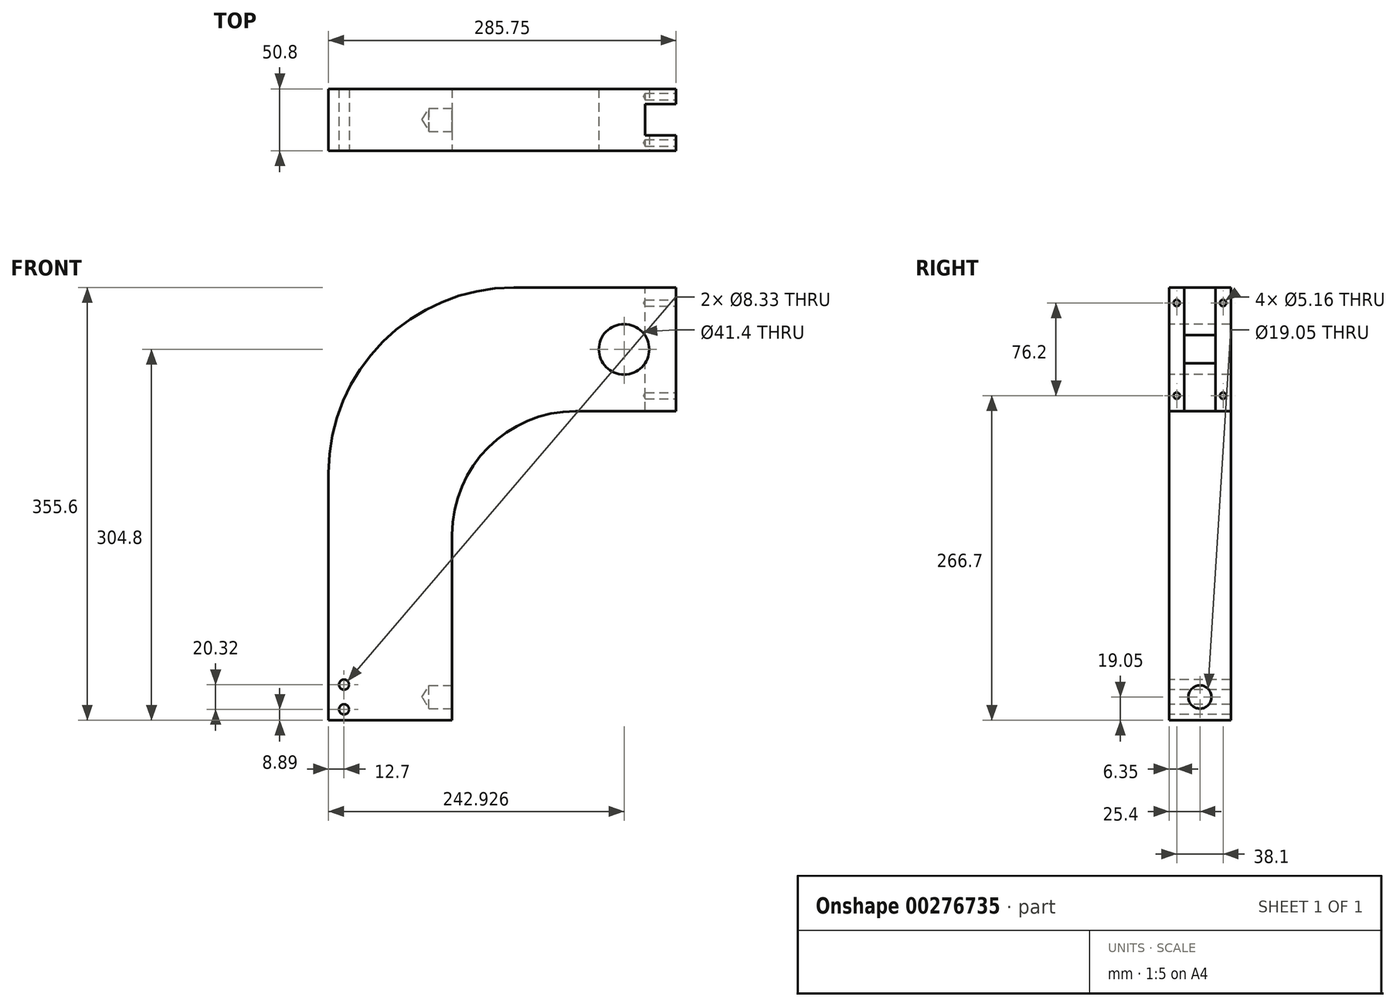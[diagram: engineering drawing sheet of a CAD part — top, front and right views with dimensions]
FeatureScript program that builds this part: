
annotation { "Feature Type Name" : "Feature", "Feature Type Description" : "" }
export const myFeature = defineFeature(function(context is Context, id is Id, definition is map)
    precondition{}
    {
        {
            var Q0;
            Q0=qCreatedBy(makeId("Front.planeOp"),FACE);
            var sketch = newSketch(context, id + "F0", { "sketchPlane" : qUnion([Q0])});
            skLineSegment(sketch, "E0", {"start": v(0, 0) * mm, "end": v(0, 203.2) * mm});
            skLineSegment(sketch, "E1", {"start": v(152.4, 355.6) * mm, "end": v(285.75, 355.6) * mm});
            skLineSegment(sketch, "E2", {"start": v(285.75, 355.6) * mm, "end": v(285.75, 254) * mm});
            skLineSegment(sketch, "E3", {"start": v(101.6, 0) * mm, "end": v(0, 0) * mm});
            skLineSegment(sketch, "E4", {"start": v(285.75, 254) * mm, "end": v(203.2, 254) * mm});
            skLineSegment(sketch, "E5", {"start": v(101.6, 0) * mm, "end": v(101.6, 152.4) * mm});
            skPoint(sketch, "E6.visualSharp", {"position": v(0, 355.6) * mm});
            skArc(sketch, "E6.filletArc", {"start": v(152.4, 355.6) * mm, "mid": v(44.64, 310.96) * mm, "end": v(0, 203.2) * mm});
            skPoint(sketch, "E7.visualSharp", {"position": v(101.6, 254) * mm});
            skArc(sketch, "E7.filletArc", {"start": v(203.2, 254) * mm, "mid": v(131.36, 224.24) * mm, "end": v(101.6, 152.4) * mm});
            skSolve(sketch);
        }
        {
            var Q0;
            Q0 = qSketchRegion(id + "F0", true);
            extrude(context, id + "F1", {"entities" : qUnion([Q0]), "oppositeDirection" : true, "depth" : 50.8 * mm});
        }
        {
            var Q0;
            Q0=makeQuery(id+"F1.opExtrude","CAP_FACE",FACE,{"disambiguationData":[OSD([sQuery(id+"F0.wireOp",EDGE,"E0"),sQuery(id+"F0.wireOp",EDGE,"E1"),sQuery(id+"F0.wireOp",EDGE,"E2"),sQuery(id+"F0.wireOp",EDGE,"E3"),sQuery(id+"F0.wireOp",EDGE,"E4"),sQuery(id+"F0.wireOp",EDGE,"E5"),sQuery(id+"F0.wireOp",EDGE,"E6.filletArc"),sQuery(id+"F0.wireOp",EDGE,"E7.filletArc")])],"isStart":true});
            var sketch = newSketch(context, id + "F2", { "sketchPlane" : qUnion([Q0])});
            skPoint(sketch, "E8", {"position": v(12.7, 29.21) * mm});
            skPoint(sketch, "E9", {"position": v(12.7, 8.9) * mm});
            skSolve(sketch);
        }
        {
            var Q0;
            Q0=sQuery(id+"F2.wireOp",VERTEX,"E8");
            var Q1;
            Q1=sQuery(id+"F2.wireOp",VERTEX,"E9");
            var Q2;
            Q2=makeQuery(id+"F1.opExtrude","SWEPT_BODY",BODY,{"disambiguationData":[OSD([sQuery(id+"F0.wireOp",EDGE,"E0"),sQuery(id+"F0.wireOp",EDGE,"E1"),sQuery(id+"F0.wireOp",EDGE,"E2"),sQuery(id+"F0.wireOp",EDGE,"E3"),sQuery(id+"F0.wireOp",EDGE,"E4"),sQuery(id+"F0.wireOp",EDGE,"E5"),sQuery(id+"F0.wireOp",EDGE,"E6.filletArc"),sQuery(id+"F0.wireOp",EDGE,"E7.filletArc")])]});
            hole(context, id + "F3", {"style" : HoleStyle.SIMPLE, "endStyle" : HoleEndStyle.THROUGH, "holeDiameter" : 8.33 * mm, "tappedDepth" : 12.7 * mm, "tapClearance" : 3, "locations" : qUnion([Q0, Q1]), "scope" : qUnion([Q2])});
        }
        {
            var Q0;
            Q0=makeQuery(id+"F1.opExtrude","SWEPT_FACE",FACE,{"disambiguationData":[OSD([sQuery(id+"F0.wireOp",EDGE,"E5")])]});
            var sketch = newSketch(context, id + "F4", { "sketchPlane" : qUnion([Q0])});
            skPoint(sketch, "E10", {"position": v(25.4, 19.05) * mm});
            skSolve(sketch);
        }
        {
            var Q0;
            Q0=sQuery(id+"F4.wireOp",VERTEX,"E10");
            var Q1;
            Q1=makeQuery(id+"F1.opExtrude","SWEPT_BODY",BODY,{"disambiguationData":[OSD([sQuery(id+"F0.wireOp",EDGE,"E0"),sQuery(id+"F0.wireOp",EDGE,"E1"),sQuery(id+"F0.wireOp",EDGE,"E2"),sQuery(id+"F0.wireOp",EDGE,"E3"),sQuery(id+"F0.wireOp",EDGE,"E4"),sQuery(id+"F0.wireOp",EDGE,"E5"),sQuery(id+"F0.wireOp",EDGE,"E6.filletArc"),sQuery(id+"F0.wireOp",EDGE,"E7.filletArc")])]});
            hole(context, id + "F5", {"style" : HoleStyle.SIMPLE, "endStyle" : HoleEndStyle.BLIND, "holeDiameter" : 19.05 * mm, "holeDepth" : 19.05 * mm, "tappedDepth" : 12.7 * mm, "tapClearance" : 3, "locations" : qUnion([Q0]), "scope" : qUnion([Q1])});
        }
        {
            var Q0;
            Q0=makeQuery(id+"F1.opExtrude","SWEPT_FACE",FACE,{"disambiguationData":[OSD([sQuery(id+"F0.wireOp",EDGE,"E1")])]});
            var sketch = newSketch(context, id + "F6", { "sketchPlane" : qUnion([Q0])});
            skLineSegment(sketch, "E11", {"start": v(285.75, 25.4) * mm, "end": v(0, 25.4) * mm, "construction": true});
            skLineSegment(sketch, "E12.bottom", {"start": v(285.75, 38.23) * mm, "end": v(260.1, 38.23) * mm});
            skLineSegment(sketch, "E12.top", {"start": v(285.75, 12.57) * mm, "end": v(260.1, 12.57) * mm});
            skLineSegment(sketch, "E12.left", {"start": v(285.75, 38.23) * mm, "end": v(285.75, 12.57) * mm});
            skLineSegment(sketch, "E12.right", {"start": v(260.1, 38.23) * mm, "end": v(260.1, 12.57) * mm});
            skSolve(sketch);
        }
        {
            var Q0;
            Q0 = qSketchRegion(id + "F6", true);
            extrude(context, id + "F7", {"entities" : qUnion([Q0]), "operationType" : NewBodyOperationType.REMOVE, "endBound" : BoundingType.THROUGH_ALL, "oppositeDirection" : true, "depth" : 25.4 * mm});
        }
        {
            var Q0;
            Q0=makeQuery(id+"F1.opExtrude","CAP_FACE",FACE,{"disambiguationData":[OSD([sQuery(id+"F0.wireOp",EDGE,"E0"),sQuery(id+"F0.wireOp",EDGE,"E1"),sQuery(id+"F0.wireOp",EDGE,"E2"),sQuery(id+"F0.wireOp",EDGE,"E3"),sQuery(id+"F0.wireOp",EDGE,"E4"),sQuery(id+"F0.wireOp",EDGE,"E5"),sQuery(id+"F0.wireOp",EDGE,"E6.filletArc"),sQuery(id+"F0.wireOp",EDGE,"E7.filletArc")])],"isStart":true});
            var sketch = newSketch(context, id + "F8", { "sketchPlane" : qUnion([Q0])});
            skCircle(sketch, "E13", {"center": v(242.93, 304.8) * mm, "radius": 20.7 * mm});
            skSolve(sketch);
        }
        {
            var Q0;
            Q0 = qSketchRegion(id + "F8", true);
            extrude(context, id + "F9", {"entities" : qUnion([Q0]), "operationType" : NewBodyOperationType.REMOVE, "endBound" : BoundingType.THROUGH_ALL, "oppositeDirection" : true, "depth" : 25.4 * mm});
        }
        {
            var Q0;
            {var subQ1=sQuery(id+"F0.wireOp",EDGE,"E2");Q0=makeQuery(id+"F7.boolean.opBoolean","SPLIT",FACE,{"disambiguationData":[TD([makeQuery(id+"F7.opExtrude","SWEPT_FACE",FACE,{"disambiguationData":[OSD([sQuery(id+"F6.wireOp",EDGE,"E12.top")])]})])],"derivedFrom":makeQuery(id+"F1.opExtrude","SWEPT_FACE",FACE,{"disambiguationData":[OSD([subQ1])]})});}
            var sketch = newSketch(context, id + "F10", { "sketchPlane" : qUnion([Q0])});
            skPoint(sketch, "E14", {"position": v(6.35, 342.9) * mm});
            skPoint(sketch, "E15", {"position": v(44.45, 342.9) * mm});
            skPoint(sketch, "E16", {"position": v(6.35, 266.7) * mm});
            skPoint(sketch, "E17", {"position": v(44.45, 266.7) * mm});
            skLineSegment(sketch, "E18.0", {"start": v(50.8, 0) * mm, "end": v(0, 0) * mm, "construction": true});
            skLineSegment(sketch, "E19.0", {"start": v(0, 355.6) * mm, "end": v(0, 254) * mm, "construction": true});
            skLineSegment(sketch, "E20", {"start": v(25.4, 0) * mm, "end": v(25.4, 364.03) * mm, "construction": true});
            skLineSegment(sketch, "E21", {"start": v(0, 304.8) * mm, "end": v(96.81, 304.8) * mm, "construction": true});
            skSolve(sketch);
        }
        {
            var Q0;
            Q0=sQuery(id+"F10.wireOp",VERTEX,"E14");
            var Q1;
            Q1=sQuery(id+"F10.wireOp",VERTEX,"E15");
            var Q2;
            Q2=sQuery(id+"F10.wireOp",VERTEX,"E16");
            var Q3;
            Q3=sQuery(id+"F10.wireOp",VERTEX,"E17");
            var Q4;
            Q4=makeQuery(id+"F1.opExtrude","SWEPT_BODY",BODY,{"disambiguationData":[OSD([sQuery(id+"F0.wireOp",EDGE,"E0"),sQuery(id+"F0.wireOp",EDGE,"E1"),sQuery(id+"F0.wireOp",EDGE,"E2"),sQuery(id+"F0.wireOp",EDGE,"E3"),sQuery(id+"F0.wireOp",EDGE,"E4"),sQuery(id+"F0.wireOp",EDGE,"E5"),sQuery(id+"F0.wireOp",EDGE,"E6.filletArc"),sQuery(id+"F0.wireOp",EDGE,"E7.filletArc")])]});
            hole(context, id + "F11", {"style" : HoleStyle.SIMPLE, "endStyle" : HoleEndStyle.BLIND, "holeDiameter" : 5.16 * mm, "holeDepth" : 25.4 * mm, "tappedDepth" : 12.7 * mm, "tapClearance" : 3, "locations" : qUnion([Q0, Q1, Q2, Q3]), "scope" : qUnion([Q4])});
        }
    });
